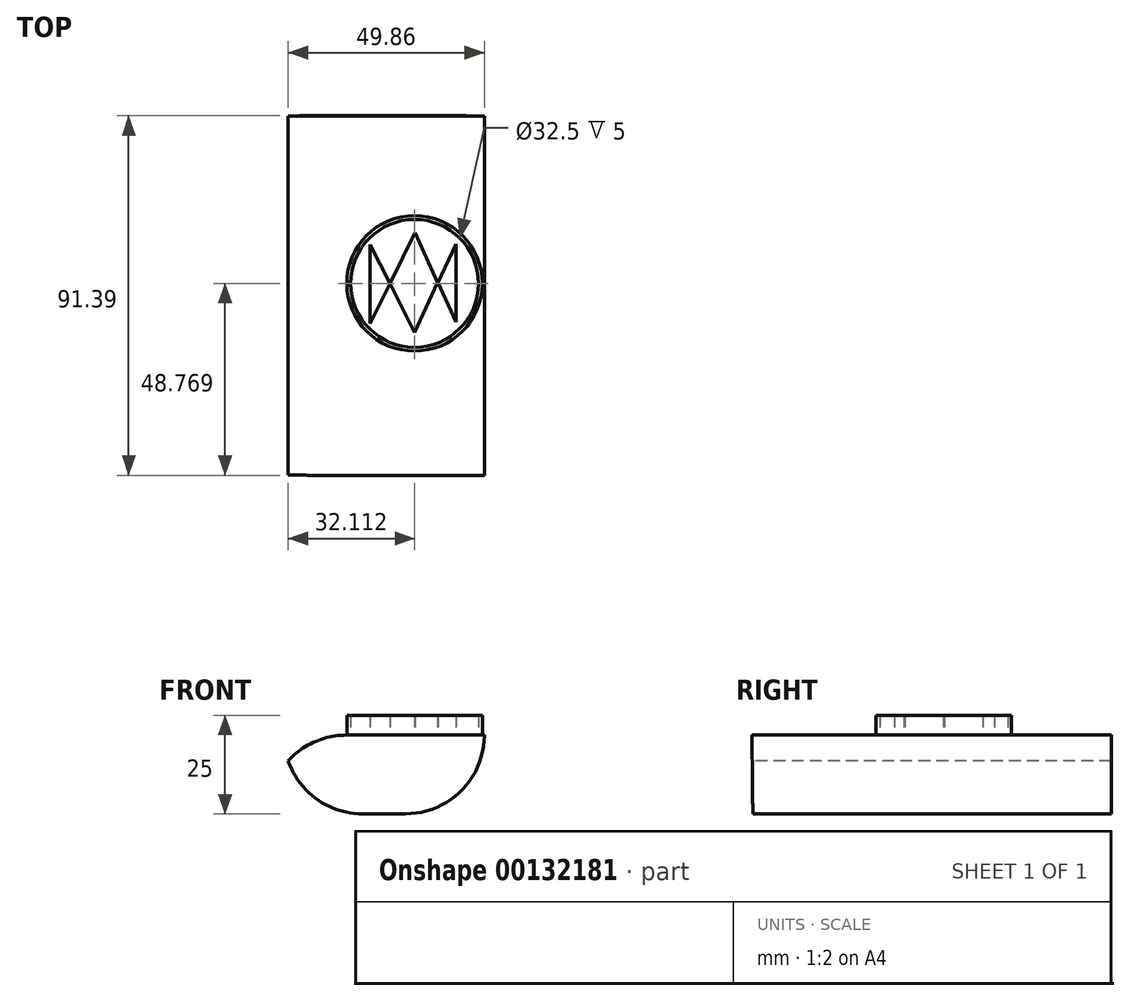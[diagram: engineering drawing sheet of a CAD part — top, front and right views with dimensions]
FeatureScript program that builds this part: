
annotation { "Feature Type Name" : "Feature", "Feature Type Description" : "" }
export const myFeature = defineFeature(function(context is Context, id is Id, definition is map)
    precondition{}
    {
        {
            var Q0;
            Q0=qCreatedBy(makeId("Top.planeOp"),FACE);
            var sketch = newSketch(context, id + "F0", { "sketchPlane" : qUnion([Q0])});
            skLineSegment(sketch, "E0.bottom", {"start": v(-27.58, 39.6) * mm, "end": v(34.43, 39.6) * mm});
            skLineSegment(sketch, "E0.top", {"start": v(-27.58, -51.55) * mm, "end": v(34.43, -51.55) * mm});
            skLineSegment(sketch, "E0.left", {"start": v(-27.58, 39.6) * mm, "end": v(-27.58, -51.55) * mm});
            skLineSegment(sketch, "E0.right", {"start": v(34.43, 39.6) * mm, "end": v(34.43, -51.55) * mm});
            skSolve(sketch);
        }
        {
            var Q0;
            Q0=makeQuery(id+"F0.imprint","IMPRINT",FACE,{"disambiguationData":[TD([[makeQuery(id+"F0.imprint","IMPRINT",EDGE,{"derivedFrom":sQuery(id+"F0.wireOp",EDGE,"E0.bottom")}),-1.0]])]});
            cPlane(context, id + "F1", {"entities" : qUnion([Q0]), "cplaneType" : CPlaneType.OFFSET, "offset" : 20 * mm, "width" : 150 * mm, "height" : 150 * mm});
        }
        {
            var Q0;
            Q0=qCreatedBy(id+"F1.planeOp",FACE);
            var sketch = newSketch(context, id + "F2", { "sketchPlane" : qUnion([Q0])});
            skLineSegment(sketch, "E1.bottom", {"start": v(-9.34, 39.5) * mm, "end": v(34.58, 39.5) * mm});
            skLineSegment(sketch, "E1.top", {"start": v(-9.34, -51.78) * mm, "end": v(34.58, -51.78) * mm});
            skLineSegment(sketch, "E1.left", {"start": v(-9.34, 39.5) * mm, "end": v(-9.34, -51.78) * mm});
            skLineSegment(sketch, "E1.right", {"start": v(34.58, 39.5) * mm, "end": v(34.58, -51.78) * mm});
            skSolve(sketch);
        }
        {
            var Q0;
            Q0=makeQuery(id+"F0.imprint","IMPRINT",FACE,{"disambiguationData":[TD([[makeQuery(id+"F0.imprint","IMPRINT",EDGE,{"derivedFrom":sQuery(id+"F0.wireOp",EDGE,"E0.bottom")}),-1.0]])]});
            var Q1;
            Q1=makeQuery(id+"F2.imprint","IMPRINT",FACE,{"disambiguationData":[TD([[makeQuery(id+"F2.imprint","IMPRINT",EDGE,{"derivedFrom":sQuery(id+"F2.wireOp",EDGE,"E1.bottom")}),-1.0]])]});
            loft(context, id + "F3", {"sheetProfilesArray" : [{ "sheetProfileEntities" : qUnion([Q0]) }, { "sheetProfileEntities" : qUnion([Q1]) }]});
        }
        {
            var Q0;
            Q0=makeQuery(id+"F3.opLoft","MID_CAP_EDGE",EDGE,{"disambiguationData":[OSD([sQuery(id+"F2.wireOp",EDGE,"E1.bottom"),sQuery(id+"F2.wireOp",EDGE,"E1.top"),sQuery(id+"F2.wireOp",EDGE,"E1.left")])],"capPos":1.0});
            fillet(context, id + "F4", {"entities" : qUnion([Q0]), "radius" : 20 * mm, "tangentPropagation" : true, "allowEdgeOverflow" : false});
        }
        {
            var Q0;
            Q0=makeQuery(id+"F3.opLoft","MID_CAP_EDGE",EDGE,{"disambiguationData":[OSD([sQuery(id+"F0.wireOp",EDGE,"E0.bottom"),sQuery(id+"F0.wireOp",EDGE,"E0.top"),sQuery(id+"F0.wireOp",EDGE,"E0.right")])],"capPos":0.0});
            fillet(context, id + "F5", {"entities" : qUnion([Q0]), "radius" : 20 * mm, "tangentPropagation" : true, "allowEdgeOverflow" : false});
        }
        {
            var Q0;
            Q0=makeQuery(id+"F3.opLoft","MID_CAP_EDGE",EDGE,{"disambiguationData":[OSD([sQuery(id+"F0.wireOp",EDGE,"E0.bottom"),sQuery(id+"F0.wireOp",EDGE,"E0.top"),sQuery(id+"F0.wireOp",EDGE,"E0.left")])],"capPos":0.0});
            fillet(context, id + "F6", {"entities" : qUnion([Q0]), "radius" : 20 * mm, "tangentPropagation" : true, "allowEdgeOverflow" : false});
        }
        {
            var Q0;
            Q0=makeQuery(id+"F2.imprint","IMPRINT",FACE,{"disambiguationData":[TD([[makeQuery(id+"F2.imprint","IMPRINT",EDGE,{"derivedFrom":sQuery(id+"F2.wireOp",EDGE,"E1.bottom")}),-1.0]])]});
            cPlane(context, id + "F7", {"entities" : qUnion([Q0]), "cplaneType" : CPlaneType.OFFSET, "offset" : 0 * mm, "width" : 150 * mm, "height" : 150 * mm});
        }
        {
            var Q0;
            Q0=qCreatedBy(id+"F7.planeOp",FACE);
            var sketch = newSketch(context, id + "F8", { "sketchPlane" : qUnion([Q0])});
            skLineSegment(sketch, "E2", {"start": v(5.52, -13.21) * mm, "end": v(5.52, 6.85) * mm});
            skLineSegment(sketch, "E3", {"start": v(27.38, 6.93) * mm, "end": v(27.38, -12.87) * mm});
            skCircle(sketch, "E4", {"center": v(16.83, -3.01) * mm, "radius": 16.25 * mm});
            skCircle(sketch, "E5", {"center": v(16.83, -3.01) * mm, "radius": 17.2 * mm});
            skLineSegment(sketch, "E6", {"start": v(27.38, 6.93) * mm, "end": v(22.8, -2.83) * mm});
            skLineSegment(sketch, "E7", {"start": v(22.8, -2.83) * mm, "end": v(27.38, -12.87) * mm});
            skLineSegment(sketch, "E8", {"start": v(5.52, 6.85) * mm, "end": v(10.55, -3.1) * mm});
            skLineSegment(sketch, "E9", {"start": v(10.55, -3.1) * mm, "end": v(5.52, -13.21) * mm});
            skPoint(sketch, "E10.start.orphan", {"position": v(10.55, -3.1) * mm});
            skLineSegment(sketch, "E11", {"start": v(10.6, -3.1) * mm, "end": v(17, 9.85) * mm});
            skLineSegment(sketch, "E12", {"start": v(16.83, -15.53) * mm, "end": v(10.6, -3.1) * mm});
            skLineSegment(sketch, "E13", {"start": v(16.83, -15.53) * mm, "end": v(22.68, -2.83) * mm});
            skLineSegment(sketch, "E14", {"start": v(22.68, -2.83) * mm, "end": v(17, 9.85) * mm});
            skSolve(sketch);
        }
        {
            var Q0;
            Q0=makeQuery(id+"F8.imprint","IMPRINT",FACE,{"disambiguationData":[TD([[makeQuery(id+"F8.imprint","IMPRINT",EDGE,{"derivedFrom":sQuery(id+"F8.wireOp",EDGE,"E2")}),-1.0]])]});
            var Q1;
            Q1=makeQuery(id+"F8.imprint","IMPRINT",FACE,{"disambiguationData":[TD([[makeQuery(id+"F8.imprint","IMPRINT",EDGE,{"derivedFrom":sQuery(id+"F8.wireOp",EDGE,"E3")}),-1.0]])]});
            var Q2;
            Q2=makeQuery(id+"F8.imprint","IMPRINT",FACE,{"disambiguationData":[TD([[makeQuery(id+"F8.imprint","IMPRINT",EDGE,{"derivedFrom":sQuery(id+"F8.wireOp",EDGE,"E4")}),-1.0]])]});
            extrude(context, id + "F9", {"entities" : qUnion([Q0, Q1, Q2]), "operationType" : NewBodyOperationType.ADD, "depth" : 5 * mm});
        }
        {
            var Q0;
            Q0=makeQuery(id+"F8.imprint","IMPRINT",FACE,{"disambiguationData":[TD([[makeQuery(id+"F8.imprint","IMPRINT",EDGE,{"derivedFrom":sQuery(id+"F8.wireOp",EDGE,"E11")}),-1.0]])]});
            extrude(context, id + "F10", {"entities" : qUnion([Q0]), "operationType" : NewBodyOperationType.ADD, "depth" : 5 * mm});
        }
    });
